# Revit family: Interceptor-Josam-Manual-Cleaning-On_Floor-Type-60100H-Series
name_source: partatom
category: Plumbing Fixtures
revit_build: Autodesk Revit MEP 2012 (Build: 20110309_2315(x64)
units: mm (PartAtom-declared; Revit-internal decimal feet)

## types (9) — shared parameters
04 CSI = 22 40 00
Default Elevation = 48"
Description = Interceptor - Manual
Manufacturer = Josam Company
Manufacturer Fax = 800-627-0008
Material Finesh = Plastic - Josam - Cast Iron
Model = 60100H
Product Line = Josam
Product Page URL = http://www.josam.com
Product Type = Manual
Subcategory = Grease Interceptor
URL = http://www.josam.com
Unit = Metal - Josam - Aluminum

## per-type parameters (varying)
| type | C | D | E | F | G | Pipe Radius | Pipe Size |
| 60102H | 8 1/4" | 3 3/8" | 14 7/8" | 13" | 11 5/8" | 1" | 2" |
| 60103H | 8 1/2" | 3 3/8" | 16 5/8" | 14 1/2" | 11 7/8" | 1" | 2" |
| 60104H | 9 1/2" | 3 3/8" | 20 3/8" | 17" | 12 7/8" | 1" | 2" |
| 60105H | 12" | 4 7/8" | 20 7/8" | 19" | 16 7/8" | 1 1/2" | 3" |
| 60106H | 13" | 4 7/8" | 23 3/8" | 21 1/2" | 17 7/8" | 1 1/2" | 3" |
| 60107H | 14 1/2" | 4 7/8" | 26 1/8" | 23" | 19 3/8" | 1 1/2" | 3" |
| 60108H | 16 1/2" | 4 7/8" | 27 7/8" | 25 1/2" | 21 3/8" | 1 1/2" | 3" |
| 60109H | 21" | 6" | 41" | 31" | 27" | 1 1/2" | 3" |
| 60110H | 23" | 8" | 47" | 35" | 31" | 2" | 4" |

## geometry (parser evidence)
native form markers: Blend x6, Sweep x5
no freeform markers — native parametric forms only
